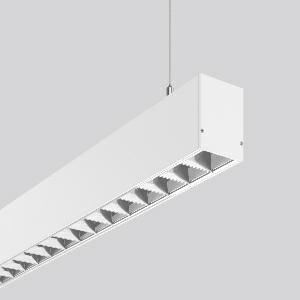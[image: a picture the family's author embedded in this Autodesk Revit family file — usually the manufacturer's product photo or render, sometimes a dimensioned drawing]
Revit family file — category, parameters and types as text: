
# Revit family: less_is_more_50_312342_002_1_baf6
name_source: partatom
category: Lighting Fixtures
units: mm (PartAtom-declared; Revit-internal decimal feet)

## family parameters
Cut with Voids When Loaded = No
Host = Face
Light Source = No
Part Type = Normal
Room Calculation Point = No
Round Connector Dimension = Use Diameter
Shared = No

## types (1)
- LESS IS MORE 50 (1 x LED Modul 840, 5050 lm, 4000)
    Apparent Load = 46 VA
    CIE Flux Codes = 95 100 100 63 100
    Color Rendering = 80
    Color Temperature = 4000
    Default Elevation = 1800 mm
    Description = Series: LESS IS MORE 50
Linear pendant luminaire for aesthetically sophisticated lighting. Housing: extruded aluminium profile, powder-coated. End cap aluminium powder-coated. Canopy made of aluminium, powder-coated. Alea optical system: Reflector structure (ABS, Aluminium-coated, highly polished) with integrated diffuser made of non-yellowing plastic (PMMA) opal for glare-free light at the workstation (screen-compliant according to EN 12464-1). Direct 65%, indirect 35% light emission. Suitable for pendant. 2-point steel cable suspension freely positionable and infinitely height-adjustable. Special lengths available on request. LED unit with integrated converter interchangeable and removable. Suitable for through-wiring. With sensors or as a safety luminaire on request. 
Colour: traffic white, matt (RAL 9016)
Length: 1127 mm
Width: 57 mm
Height: 75 mm
Suspension length: 2000 mm
Lamp: LED
Socket: without socket
Colour temperature: 4000K
Colour rendering index (CRI): 80
Light source: LED
Socket lamp2: Without base
Colour temperature: 4000K
System power: 46 W
Rated luminous flux: 5050 lm
Luminous efficiency: 110 lm/W
Control gear: Regulated power supply
Control gear: Regulated power supply
Protection class: I
Type of protection: IP 20
    Height = 75 mm
    Lamp = 1 x LED Modul 840
    Lamp Light Flux = 5050 lm
    Lamp count = 1
    Length = 1127 mm
    Lifetime = 50000 h
    Luminous efficacy = 110 lm/W
    Manufacturer = RZB
    ModVariant = No
    Model = 312342.002.1
    Mounting Place = Ceiling
    Mounting Type = Pendant
    Number of Poles = 1
    OnlyDefault = Yes
    Power Factor = 1
    Product Name = LESS IS MORE 50
    Product group = Pendant LED linear luminaires
    ProductGroupID = 907
    Protection Class = Protection class I
    Protection Degree = IP 20
    RLX_Detail_Level = 1
    RLX_Emergency_Light_Flux = 0 lm
    RLX_Emergency_Type = 0
    RLX_Emergency_Type_DB = No
    RlxData = <blob elided: 37465 chars, md5=e311bd3e>
    Socket = socket
    Standby Power = 0 W
    System Light Flux = 5050 lm
    System Power = 46 W
    Type Comments = Product without accessories
    Type Image = 312342.002.jpg
    URL = http://relux.com
    VarID = ---
    Voltage = 230 V
    Voltage Range = 220-240 V
    Weight = 0.00 kg
    Width = 57 mm

## geometry (parser evidence)
native form markers: Blend x4, Sweep x11
no freeform markers — native parametric forms only
